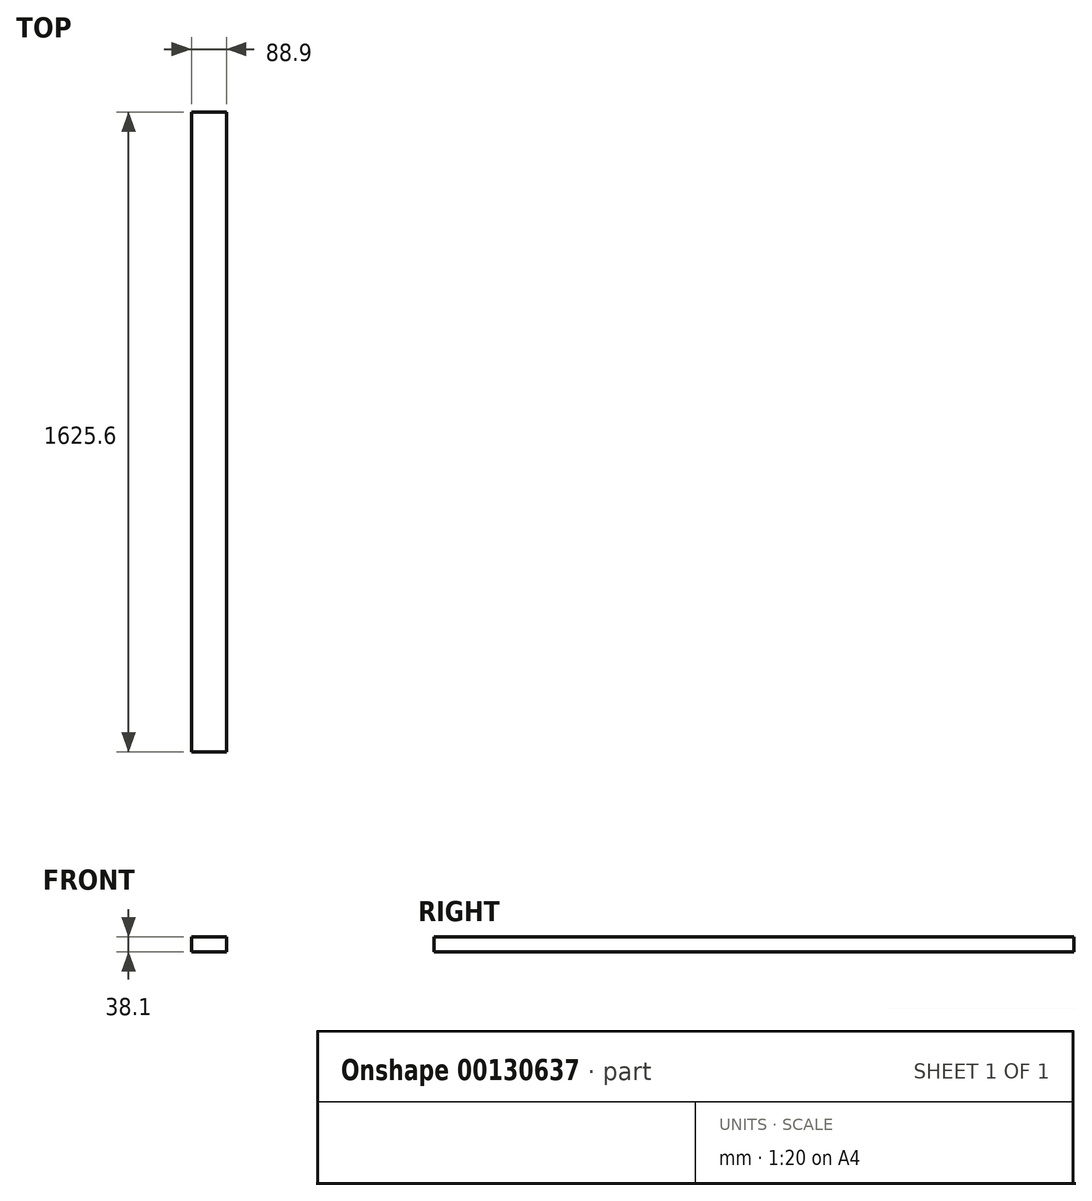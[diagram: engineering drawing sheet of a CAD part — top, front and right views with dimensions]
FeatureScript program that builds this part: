
annotation { "Feature Type Name" : "Feature", "Feature Type Description" : "" }
export const myFeature = defineFeature(function(context is Context, id is Id, definition is map)
    precondition{}
    {
        {
            var Q0;
            Q0=qCreatedBy(makeId("Top.planeOp"),FACE);
            var sketch = newSketch(context, id + "F0", { "sketchPlane" : qUnion([Q0])});
            skLineSegment(sketch, "E0.bottom", {"start": v(0, 0) * mm, "end": v(88.9, 0) * mm});
            skLineSegment(sketch, "E0.top", {"start": v(0, 1625.6) * mm, "end": v(88.9, 1625.6) * mm});
            skLineSegment(sketch, "E0.left", {"start": v(0, 0) * mm, "end": v(0, 1625.6) * mm});
            skLineSegment(sketch, "E0.right", {"start": v(88.9, 0) * mm, "end": v(88.9, 1625.6) * mm});
            skSolve(sketch);
        }
        {
            var Q0;
            Q0=makeQuery(id+"F0.imprint","IMPRINT",FACE,{"disambiguationData":[TD([[makeQuery(id+"F0.imprint","IMPRINT",EDGE,{"derivedFrom":sQuery(id+"F0.wireOp",EDGE,"E0.bottom")}),1.0]])]});
            extrude(context, id + "F1", {"entities" : qUnion([Q0]), "depth" : 38.1 * mm});
        }
    });
